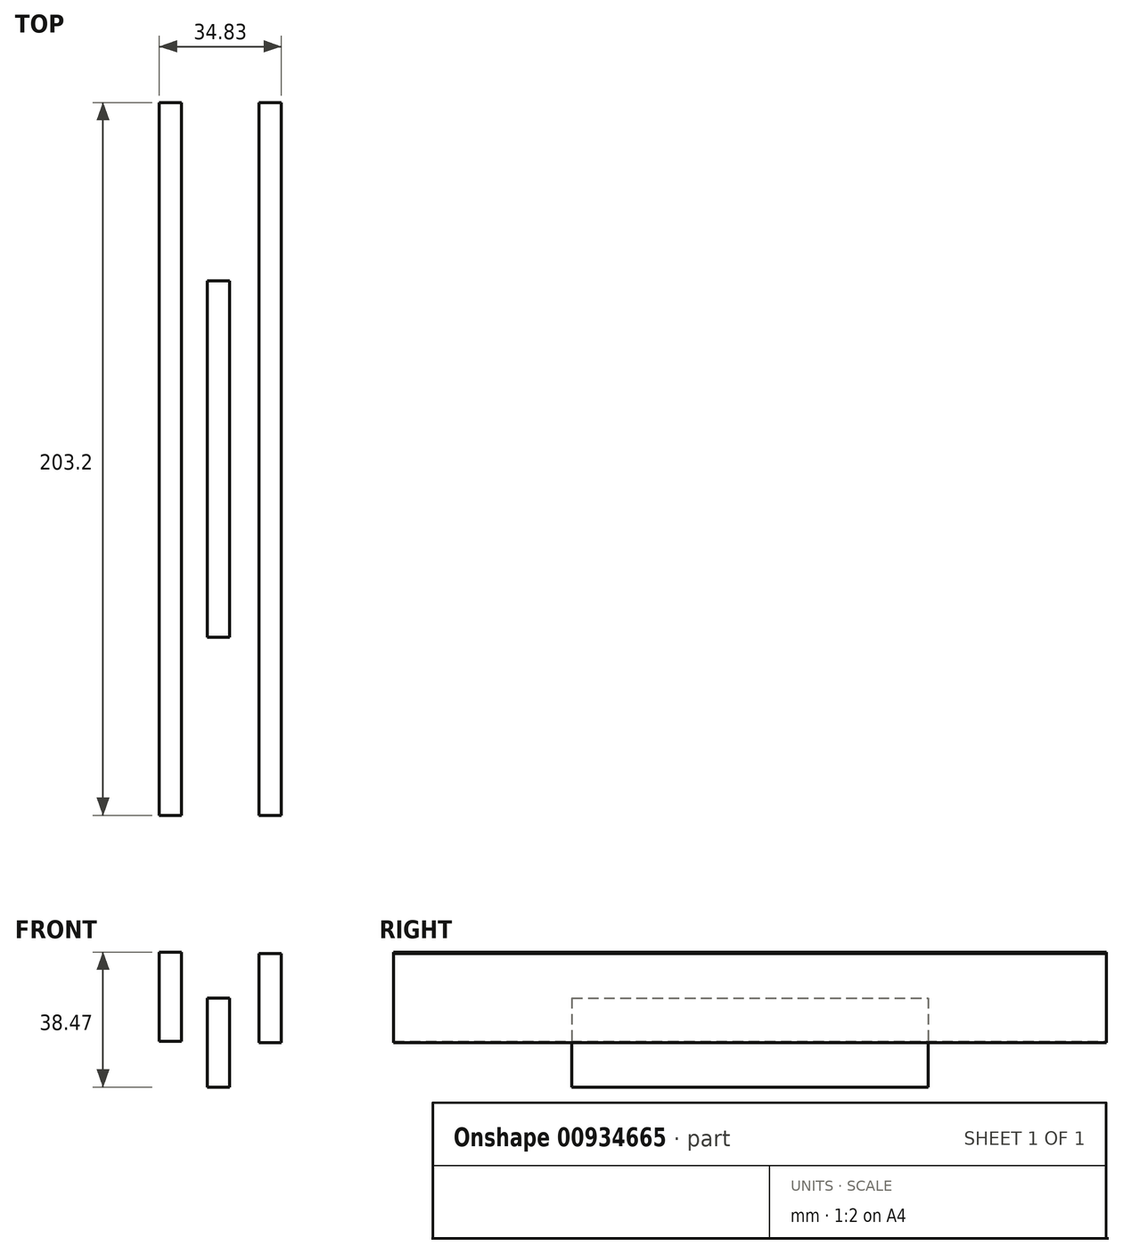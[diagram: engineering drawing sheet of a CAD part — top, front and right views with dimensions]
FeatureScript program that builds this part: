
annotation { "Feature Type Name" : "Feature", "Feature Type Description" : "" }
export const myFeature = defineFeature(function(context is Context, id is Id, definition is map)
    precondition{}
    {
        {
            var Q0;
            Q0=qCreatedBy(makeId("Front.planeOp"),FACE);
            var sketch = newSketch(context, id + "F0", { "sketchPlane" : qUnion([Q0])});
            skLineSegment(sketch, "E0.bottom", {"start": v(17.93, 25.37) * mm, "end": v(11.58, 25.37) * mm});
            skLineSegment(sketch, "E0.top", {"start": v(17.93, -0.03) * mm, "end": v(11.58, -0.03) * mm});
            skLineSegment(sketch, "E0.left", {"start": v(17.93, 25.37) * mm, "end": v(17.93, -0.03) * mm});
            skLineSegment(sketch, "E0.right", {"start": v(11.58, 25.37) * mm, "end": v(11.58, -0.03) * mm});
            skSolve(sketch);
        }
        {
            var Q0;
            Q0=makeQuery(id+"F0.imprint","IMPRINT",FACE,{"disambiguationData":[TD([[makeQuery(id+"F0.imprint","IMPRINT",EDGE,{"derivedFrom":sQuery(id+"F0.wireOp",EDGE,"E0.bottom")}),1.0]])]});
            extrude(context, id + "F1", {"entities" : qUnion([Q0]), "endBound" : BoundingType.SYMMETRIC, "depth" : 203.2 * mm, "offsetDistance" : 25.4 * mm});
        }
        {
            var Q0;
            Q0=qCreatedBy(makeId("Front.planeOp"),FACE);
            var sketch = newSketch(context, id + "F2", { "sketchPlane" : qUnion([Q0])});
            skLineSegment(sketch, "E1.bottom", {"start": v(-10.55, 25.77) * mm, "end": v(-16.9, 25.77) * mm});
            skLineSegment(sketch, "E1.top", {"start": v(-10.55, 0.37) * mm, "end": v(-16.9, 0.37) * mm});
            skLineSegment(sketch, "E1.left", {"start": v(-10.55, 25.77) * mm, "end": v(-10.55, 0.37) * mm});
            skLineSegment(sketch, "E1.right", {"start": v(-16.9, 25.77) * mm, "end": v(-16.9, 0.37) * mm});
            skSolve(sketch);
        }
        {
            var Q0;
            Q0=qCreatedBy(makeId("Front.planeOp"),FACE);
            var sketch = newSketch(context, id + "F3", { "sketchPlane" : qUnion([Q0])});
            skLineSegment(sketch, "E2.bottom", {"start": v(3.18, 12.7) * mm, "end": v(-3.18, 12.7) * mm});
            skLineSegment(sketch, "E2.top", {"start": v(3.18, -12.7) * mm, "end": v(-3.18, -12.7) * mm});
            skLineSegment(sketch, "E2.left", {"start": v(3.17, 12.7) * mm, "end": v(3.18, -12.7) * mm});
            skLineSegment(sketch, "E2.right", {"start": v(-3.18, 12.7) * mm, "end": v(-3.18, -12.7) * mm});
            skSolve(sketch);
        }
        {
            var Q0;
            Q0 = qSketchRegion(id + "F2", true);
            extrude(context, id + "F4", {"entities" : qUnion([Q0]), "endBound" : BoundingType.SYMMETRIC, "depth" : 203.2 * mm, "offsetDistance" : 25.4 * mm});
        }
        {
            var Q0;
            Q0=makeQuery(id+"F3.imprint","IMPRINT",FACE,{"disambiguationData":[TD([[makeQuery(id+"F3.imprint","IMPRINT",EDGE,{"derivedFrom":sQuery(id+"F3.wireOp",EDGE,"E2.bottom")}),1.0]])]});
            extrude(context, id + "F5", {"entities" : qUnion([Q0]), "endBound" : BoundingType.SYMMETRIC, "depth" : 101.6 * mm, "offsetDistance" : 25.4 * mm});
        }
    });
